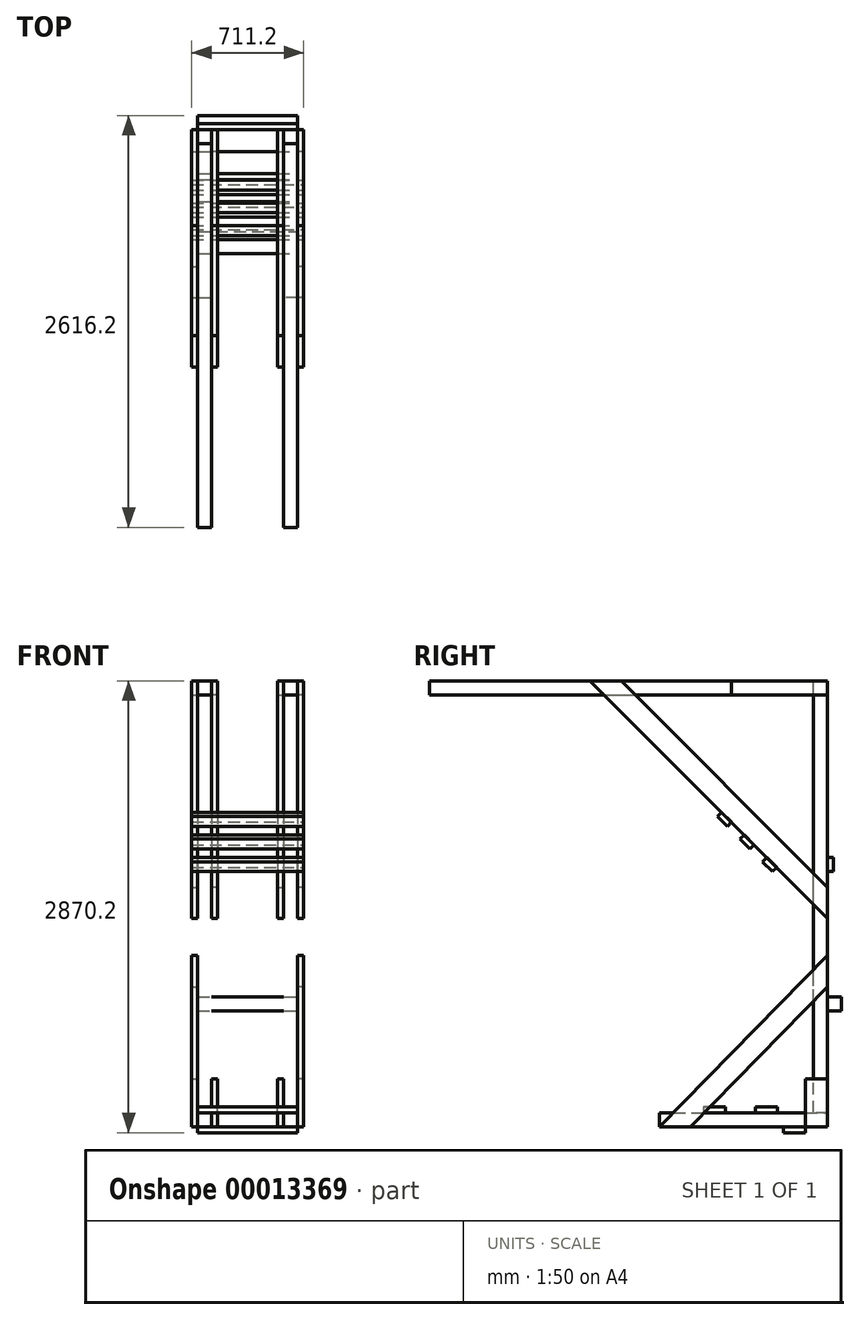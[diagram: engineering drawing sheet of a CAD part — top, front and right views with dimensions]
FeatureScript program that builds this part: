
annotation { "Feature Type Name" : "Feature", "Feature Type Description" : "" }
export const myFeature = defineFeature(function(context is Context, id is Id, definition is map)
    precondition{}
    {
        {
            var Q0;
            Q0=qCreatedBy(makeId("Top.planeOp"),FACE);
            var sketch = newSketch(context, id + "F0", { "sketchPlane" : qUnion([Q0])});
            skLineSegment(sketch, "E0.bottom", {"start": v(-317.5, 0) * mm, "end": v(-228.6, 0) * mm});
            skLineSegment(sketch, "E0.top", {"start": v(-317.5, -88.9) * mm, "end": v(-228.6, -88.9) * mm});
            skLineSegment(sketch, "E0.left", {"start": v(-317.5, 0) * mm, "end": v(-317.5, -88.9) * mm});
            skLineSegment(sketch, "E0.right", {"start": v(-228.6, 0) * mm, "end": v(-228.6, -88.9) * mm});
            skSolve(sketch);
        }
        {
            var Q0;
            Q0=qSketchRegion(id+"F0",true);
            extrude(context, id + "F1", {"entities" : qUnion([Q0]), "oppositeDirection" : true, "depth" : 2743.2 * mm});
        }
        {
            var Q0;
            Q0=makeQuery(id+"F1.opExtrude","SWEPT_FACE",FACE,{"disambiguationData":[OSD([sQuery(id+"F0.wireOp",EDGE,"E0.bottom")])]});
            var sketch = newSketch(context, id + "F2", { "sketchPlane" : qUnion([Q0])});
            skLineSegment(sketch, "E1.bottom", {"start": v(317.5, -2832.1) * mm, "end": v(228.6, -2832.1) * mm});
            skLineSegment(sketch, "E1.top", {"start": v(317.5, -2743.2) * mm, "end": v(228.6, -2743.2) * mm});
            skLineSegment(sketch, "E1.left", {"start": v(228.6, -2832.1) * mm, "end": v(228.6, -2743.2) * mm});
            skLineSegment(sketch, "E1.right", {"start": v(317.5, -2832.1) * mm, "end": v(317.5, -2743.2) * mm});
            skSolve(sketch);
        }
        {
            var Q0;
            Q0=makeQuery(id+"F2.imprint","IMPRINT",FACE,{"disambiguationData":[TD([[makeQuery(id+"F2.imprint","IMPRINT",EDGE,{"derivedFrom":sQuery(id+"F2.wireOp",EDGE,"E1.bottom")}),-1.0]])]});
            extrude(context, id + "F3", {"entities" : qUnion([Q0]), "oppositeDirection" : true, "depth" : 1066.8 * mm});
        }
        {
            var Q0;
            Q0=makeQuery(id+"F1.opExtrude","SWEPT_FACE",FACE,{"disambiguationData":[OSD([sQuery(id+"F0.wireOp",EDGE,"E0.right")])]});
            var sketch = newSketch(context, id + "F4", { "sketchPlane" : qUnion([Q0])});
            skLineSegment(sketch, "E2.bottom", {"start": v(0, -2832.1) * mm, "end": v(-139.7, -2832.1) * mm});
            skLineSegment(sketch, "E2.top", {"start": v(0, -2527.3) * mm, "end": v(-139.7, -2527.3) * mm});
            skLineSegment(sketch, "E2.left", {"start": v(0, -2832.1) * mm, "end": v(0, -2527.3) * mm});
            skLineSegment(sketch, "E2.right", {"start": v(-139.7, -2832.1) * mm, "end": v(-139.7, -2527.3) * mm});
            skSolve(sketch);
        }
        {
            var Q0;
            {var subQ5=sQuery(id+"F4.wireOp",EDGE,"E2.right");Q0=makeQuery(id+"F4.imprint","IMPRINT",FACE,{"disambiguationData":[TD([[makeQuery(id+"F4.imprint","IMPRINT",EDGE,{"derivedFrom":subQ5}),-1.0]])]});}
            var Q1;
            {var subQ6=sQuery(id+"F4.wireOp",EDGE,"E2.left");Q1=makeQuery(id+"F4.imprint","IMPRINT",FACE,{"disambiguationData":[TD([[makeQuery(id+"F4.imprint","IMPRINT",EDGE,{"derivedFrom":subQ6}),1.0]])]});}
            extrude(context, id + "F5", {"entities" : qUnion([Q0, Q1]), "depth" : 38.1 * mm});
        }
        {
            var Q0;
            Q0=makeQuery(id+"F1.opExtrude","SWEPT_FACE",FACE,{"disambiguationData":[OSD([sQuery(id+"F0.wireOp",EDGE,"E0.top")])]});
            var sketch = newSketch(context, id + "F6", { "sketchPlane" : qUnion([Q0])});
            skLineSegment(sketch, "E3.bottom", {"start": v(-317.5, 0) * mm, "end": v(-228.6, 0) * mm});
            skLineSegment(sketch, "E3.top", {"start": v(-317.5, -88.9) * mm, "end": v(-228.6, -88.9) * mm});
            skLineSegment(sketch, "E3.left", {"start": v(-317.5, 0) * mm, "end": v(-317.5, -88.9) * mm});
            skLineSegment(sketch, "E3.right", {"start": v(-228.6, 0) * mm, "end": v(-228.6, -88.9) * mm});
            skSolve(sketch);
        }
        {
            var Q0;
            Q0=makeQuery(id+"F6.imprint","IMPRINT",FACE,{"disambiguationData":[TD([[makeQuery(id+"F6.imprint","IMPRINT",EDGE,{"derivedFrom":sQuery(id+"F6.wireOp",EDGE,"E3.bottom")}),-1.0]])]});
            extrude(context, id + "F7", {"entities" : qUnion([Q0]), "depth" : 2438.4 * mm});
        }
        {
            var Q0;
            Q0=makeQuery(id+"F1.opExtrude","SWEPT_FACE",FACE,{"disambiguationData":[OSD([sQuery(id+"F0.wireOp",EDGE,"E0.right")])]});
            var sketch = newSketch(context, id + "F8", { "sketchPlane" : qUnion([Q0])});
            skLineSegment(sketch, "E4.bottom", {"start": v(0, 0) * mm, "end": v(-609.6, 0) * mm});
            skLineSegment(sketch, "E4.top", {"start": v(0, -88.9) * mm, "end": v(-609.6, -88.9) * mm});
            skLineSegment(sketch, "E4.left", {"start": v(0, 0) * mm, "end": v(0, -88.9) * mm});
            skLineSegment(sketch, "E4.right", {"start": v(-609.6, 0) * mm, "end": v(-609.6, -88.9) * mm});
            skLineSegment(sketch, "E5.0", {"start": v(-2527.3, -88.9) * mm, "end": v(-88.9, -88.9) * mm, "construction": true});
            skSolve(sketch);
        }
        {
            var Q0;
            {var subQ5=sQuery(id+"F8.wireOp",EDGE,"E4.right");Q0=makeQuery(id+"F8.imprint","IMPRINT",FACE,{"disambiguationData":[TD([[makeQuery(id+"F8.imprint","IMPRINT",EDGE,{"derivedFrom":subQ5}),1.0]])]});}
            var Q1;
            {var subQ6=sQuery(id+"F8.wireOp",EDGE,"E4.left");Q1=makeQuery(id+"F8.imprint","IMPRINT",FACE,{"disambiguationData":[TD([[makeQuery(id+"F8.imprint","IMPRINT",EDGE,{"derivedFrom":subQ6}),1.0]])]});}
            extrude(context, id + "F9", {"entities" : qUnion([Q0, Q1]), "depth" : 38.1 * mm});
        }
        {
            var Q0;
            Q0=makeQuery(id+"F7.opExtrude","SWEPT_FACE",FACE,{"disambiguationData":[OSD([sQuery(id+"F6.wireOp",EDGE,"E3.right")])]});
            var sketch = newSketch(context, id + "F10", { "sketchPlane" : qUnion([Q0])});
            skLineSegment(sketch, "E6.0", {"start": v(0, -2743.2) * mm, "end": v(0, 0) * mm, "construction": true});
            skLineSegment(sketch, "E7", {"start": v(-1508.68, 0) * mm, "end": v(0, -1508.68) * mm});
            skLineSegment(sketch, "E8", {"start": v(0, -1508.68) * mm, "end": v(0, -1311.12) * mm});
            skLineSegment(sketch, "E9", {"start": v(0, -1311.12) * mm, "end": v(-1311.12, 0) * mm});
            skLineSegment(sketch, "E10", {"start": v(-1311.12, 0) * mm, "end": v(-1508.68, 0) * mm});
            skLineSegment(sketch, "E11", {"start": v(-1311.12, 0) * mm, "end": v(0, 0) * mm, "construction": true});
            skLineSegment(sketch, "E12", {"start": v(0, -1311.12) * mm, "end": v(0, 0) * mm, "construction": true});
            skSolve(sketch);
        }
        {
            var Q0;
            Q0=makeQuery(id+"F7.opExtrude","SWEPT_FACE",FACE,{"disambiguationData":[OSD([sQuery(id+"F6.wireOp",EDGE,"E3.right")])]});
            var Q1;
            Q1=makeQuery(id+"F7.opExtrude","SWEPT_FACE",FACE,{"disambiguationData":[OSD([sQuery(id+"F6.wireOp",EDGE,"E3.left")])]});
            cPlane(context, id + "F11", {"entities" : qUnion([Q0, Q1]), "cplaneType" : CPlaneType.MID_PLANE, "offset" : 152.4 * mm, "width" : 152.4 * mm, "height" : 152.4 * mm});
        }
        {
            var Q0;
            {var subQ5=sQuery(id+"F10.wireOp",EDGE,"E8");Q0=makeQuery(id+"F10.imprint","IMPRINT",FACE,{"disambiguationData":[TD([[makeQuery(id+"F10.imprint","IMPRINT",EDGE,{"derivedFrom":subQ5}),1.0]])]});}
            var Q1;
            {var subQ6=sQuery(id+"F10.wireOp",EDGE,"E10");Q1=makeQuery(id+"F10.imprint","IMPRINT",FACE,{"disambiguationData":[TD([[makeQuery(id+"F10.imprint","IMPRINT",EDGE,{"derivedFrom":subQ6}),-1.0]])]});}
            extrude(context, id + "F12", {"entities" : qUnion([Q0, Q1]), "depth" : 38.1 * mm});
        }
        {
            var Q0;
            Q0=makeQuery(id+"F9.opExtrude","SWEPT_BODY",BODY,{"disambiguationData":[OSD([sQuery(id+"F8.wireOp",EDGE,"E4.bottom"),sQuery(id+"F8.wireOp",EDGE,"E4.top"),sQuery(id+"F8.wireOp",EDGE,"E4.left"),sQuery(id+"F8.wireOp",EDGE,"E4.right")])]});
            var Q1;
            Q1=makeQuery(id+"F5.opExtrude","SWEPT_BODY",BODY,{"disambiguationData":[OSD([sQuery(id+"F4.wireOp",EDGE,"E2.bottom"),sQuery(id+"F4.wireOp",EDGE,"E2.top"),sQuery(id+"F4.wireOp",EDGE,"E2.left"),sQuery(id+"F4.wireOp",EDGE,"E2.right")])]});
            var Q2;
            Q2=makeQuery(id+"F12.opExtrude","SWEPT_BODY",BODY,{"disambiguationData":[OSD([sQuery(id+"F10.wireOp",EDGE,"E7"),sQuery(id+"F10.wireOp",EDGE,"E8"),sQuery(id+"F10.wireOp",EDGE,"E9"),sQuery(id+"F10.wireOp",EDGE,"E10")])]});
            var Q3;
            Q3=qCreatedBy(id+"F11.planeOp",FACE);
            mirror(context, id + "F13", {"entities" : qUnion([Q0, Q1, Q2]), "mirrorPlane" : qUnion([Q3])});
        }
        {
            var Q0;
            Q0=makeQuery(id+"F1.opExtrude","SWEPT_FACE",FACE,{"disambiguationData":[OSD([sQuery(id+"F0.wireOp",EDGE,"E0.left")])]});
            var sketch = newSketch(context, id + "F14", { "sketchPlane" : qUnion([Q0])});
            skLineSegment(sketch, "E13.0", {"start": v(1066.8, -2832.1) * mm, "end": v(0, -2832.1) * mm, "construction": true});
            skLineSegment(sketch, "E14", {"start": v(0, -1943.32) * mm, "end": v(871.18, -2832.1) * mm});
            skLineSegment(sketch, "E15", {"start": v(871.18, -2832.1) * mm, "end": v(1066.8, -2832.1) * mm});
            skLineSegment(sketch, "E16", {"start": v(1066.8, -2832.1) * mm, "end": v(0, -1743.75) * mm});
            skLineSegment(sketch, "E17", {"start": v(0, -1743.75) * mm, "end": v(0, -1943.32) * mm});
            skSolve(sketch);
        }
        {
            var Q0;
            {var subQ5=sQuery(id+"F14.wireOp",EDGE,"E15");Q0=makeQuery(id+"F14.imprint","IMPRINT",FACE,{"disambiguationData":[TD([[makeQuery(id+"F14.imprint","IMPRINT",EDGE,{"derivedFrom":subQ5}),1.0]])]});}
            var Q1;
            {var subQ6=sQuery(id+"F14.wireOp",EDGE,"E17");Q1=makeQuery(id+"F14.imprint","IMPRINT",FACE,{"disambiguationData":[TD([[makeQuery(id+"F14.imprint","IMPRINT",EDGE,{"derivedFrom":subQ6}),-1.0]])]});}
            extrude(context, id + "F15", {"entities" : qUnion([Q0, Q1]), "depth" : 38.1 * mm});
        }
        {
            var Q0;
            Q0=makeQuery(id+"F1.opExtrude","SWEPT_BODY",BODY,{"disambiguationData":[OSD([sQuery(id+"F0.wireOp",EDGE,"E0.bottom"),sQuery(id+"F0.wireOp",EDGE,"E0.top"),sQuery(id+"F0.wireOp",EDGE,"E0.left"),sQuery(id+"F0.wireOp",EDGE,"E0.right")])]});
            var Q1;
            Q1=makeQuery(id+"F3.opExtrude","SWEPT_BODY",BODY,{"disambiguationData":[OSD([sQuery(id+"F2.wireOp",EDGE,"E1.bottom"),sQuery(id+"F2.wireOp",EDGE,"E1.top"),sQuery(id+"F2.wireOp",EDGE,"E1.left"),sQuery(id+"F2.wireOp",EDGE,"E1.right")])]});
            var Q2;
            Q2=makeQuery(id+"F5.opExtrude","SWEPT_BODY",BODY,{"disambiguationData":[OSD([sQuery(id+"F4.wireOp",EDGE,"E2.bottom"),sQuery(id+"F4.wireOp",EDGE,"E2.top"),sQuery(id+"F4.wireOp",EDGE,"E2.left"),sQuery(id+"F4.wireOp",EDGE,"E2.right")])]});
            var Q3;
            Q3=makeQuery(id+"F7.opExtrude","SWEPT_BODY",BODY,{"disambiguationData":[OSD([sQuery(id+"F6.wireOp",EDGE,"E3.bottom"),sQuery(id+"F6.wireOp",EDGE,"E3.top"),sQuery(id+"F6.wireOp",EDGE,"E3.left"),sQuery(id+"F6.wireOp",EDGE,"E3.right")])]});
            var Q4;
            Q4=makeQuery(id+"F9.opExtrude","SWEPT_BODY",BODY,{"disambiguationData":[OSD([sQuery(id+"F8.wireOp",EDGE,"E4.bottom"),sQuery(id+"F8.wireOp",EDGE,"E4.top"),sQuery(id+"F8.wireOp",EDGE,"E4.left"),sQuery(id+"F8.wireOp",EDGE,"E4.right")])]});
            var Q5;
            Q5=makeQuery(id+"F13.opPattern","COPY",BODY,{"derivedFrom":makeQuery(id+"F9.opExtrude","SWEPT_BODY",BODY,{"disambiguationData":[OSD([sQuery(id+"F8.wireOp",EDGE,"E4.bottom"),sQuery(id+"F8.wireOp",EDGE,"E4.top"),sQuery(id+"F8.wireOp",EDGE,"E4.left"),sQuery(id+"F8.wireOp",EDGE,"E4.right")])]}),"instanceName":"1"});
            var Q6;
            Q6=makeQuery(id+"F13.opPattern","COPY",BODY,{"derivedFrom":makeQuery(id+"F5.opExtrude","SWEPT_BODY",BODY,{"disambiguationData":[OSD([sQuery(id+"F4.wireOp",EDGE,"E2.bottom"),sQuery(id+"F4.wireOp",EDGE,"E2.top"),sQuery(id+"F4.wireOp",EDGE,"E2.left"),sQuery(id+"F4.wireOp",EDGE,"E2.right")])]}),"instanceName":"1"});
            var Q7;
            Q7=makeQuery(id+"F15.opExtrude","SWEPT_BODY",BODY,{"disambiguationData":[OSD([sQuery(id+"F14.wireOp",EDGE,"E14"),sQuery(id+"F14.wireOp",EDGE,"E15"),sQuery(id+"F14.wireOp",EDGE,"E16"),sQuery(id+"F14.wireOp",EDGE,"E17")])]});
            var Q8;
            Q8=makeQuery(id+"F13.opPattern","COPY",BODY,{"derivedFrom":makeQuery(id+"F12.opExtrude","SWEPT_BODY",BODY,{"disambiguationData":[OSD([sQuery(id+"F10.wireOp",EDGE,"E7"),sQuery(id+"F10.wireOp",EDGE,"E8"),sQuery(id+"F10.wireOp",EDGE,"E9"),sQuery(id+"F10.wireOp",EDGE,"E10")])]}),"instanceName":"1"});
            var Q9;
            Q9=makeQuery(id+"F12.opExtrude","SWEPT_BODY",BODY,{"disambiguationData":[OSD([sQuery(id+"F10.wireOp",EDGE,"E7"),sQuery(id+"F10.wireOp",EDGE,"E8"),sQuery(id+"F10.wireOp",EDGE,"E9"),sQuery(id+"F10.wireOp",EDGE,"E10")])]});
            var Q10;
            Q10=qCreatedBy(makeId("Right.planeOp"),FACE);
            mirror(context, id + "F16", {"entities" : qUnion([Q0, Q1, Q2, Q3, Q4, Q5, Q6, Q7, Q8, Q9]), "mirrorPlane" : qUnion([Q10])});
        }
        {
            var Q0;
            Q0=makeQuery(id+"F3.opExtrude","SWEPT_FACE",FACE,{"disambiguationData":[OSD([sQuery(id+"F2.wireOp",EDGE,"E1.top")])]});
            var sketch = newSketch(context, id + "F17", { "sketchPlane" : qUnion([Q0])});
            skLineSegment(sketch, "E18.bottom", {"start": v(-317.5, -317.5) * mm, "end": v(317.5, -317.5) * mm});
            skLineSegment(sketch, "E18.top", {"start": v(-317.5, -457.2) * mm, "end": v(317.5, -457.2) * mm});
            skLineSegment(sketch, "E18.left", {"start": v(-317.5, -317.5) * mm, "end": v(-317.5, -457.2) * mm});
            skLineSegment(sketch, "E18.right", {"start": v(317.5, -317.5) * mm, "end": v(317.5, -457.2) * mm});
            skLineSegment(sketch, "E19.bottom", {"start": v(-317.5, -647.7) * mm, "end": v(317.5, -647.7) * mm});
            skLineSegment(sketch, "E19.top", {"start": v(-317.5, -787.4) * mm, "end": v(317.5, -787.4) * mm});
            skLineSegment(sketch, "E19.left", {"start": v(-317.5, -647.7) * mm, "end": v(-317.5, -787.4) * mm});
            skLineSegment(sketch, "E19.right", {"start": v(317.5, -647.7) * mm, "end": v(317.5, -787.4) * mm});
            skSolve(sketch);
        }
        {
            var Q0;
            Q0=qSketchRegion(id+"F17",true);
            extrude(context, id + "F18", {"entities" : qUnion([Q0]), "depth" : 38.1 * mm});
        }
        {
            var Q0;
            Q0=makeQuery(id+"F3.opExtrude","SWEPT_FACE",FACE,{"disambiguationData":[OSD([sQuery(id+"F2.wireOp",EDGE,"E1.bottom")])]});
            var sketch = newSketch(context, id + "F19", { "sketchPlane" : qUnion([Q0])});
            skLineSegment(sketch, "E20.bottom", {"start": v(-317.5, 139.7) * mm, "end": v(317.5, 139.7) * mm});
            skLineSegment(sketch, "E20.top", {"start": v(-317.5, 279.4) * mm, "end": v(317.5, 279.4) * mm});
            skLineSegment(sketch, "E20.left", {"start": v(-317.5, 139.7) * mm, "end": v(-317.5, 279.4) * mm});
            skLineSegment(sketch, "E20.right", {"start": v(317.5, 139.7) * mm, "end": v(317.5, 279.4) * mm});
            skSolve(sketch);
        }
        {
            var Q0;
            Q0=qSketchRegion(id+"F19",true);
            extrude(context, id + "F20", {"entities" : qUnion([Q0]), "depth" : 38.1 * mm});
        }
        {
            var Q0;
            Q0=makeQuery(id+"F1.opExtrude","SWEPT_FACE",FACE,{"disambiguationData":[OSD([sQuery(id+"F0.wireOp",EDGE,"E0.bottom")])]});
            var sketch = newSketch(context, id + "F21", { "sketchPlane" : qUnion([Q0])});
            skLineSegment(sketch, "E21.bottom", {"start": v(317.5, -2006.6) * mm, "end": v(-317.5, -2006.6) * mm});
            skLineSegment(sketch, "E21.top", {"start": v(317.5, -2095.5) * mm, "end": v(-317.5, -2095.5) * mm});
            skLineSegment(sketch, "E21.left", {"start": v(317.5, -2006.6) * mm, "end": v(317.5, -2095.5) * mm});
            skLineSegment(sketch, "E21.right", {"start": v(-317.5, -2006.6) * mm, "end": v(-317.5, -2095.5) * mm});
            skSolve(sketch);
        }
        {
            var Q0;
            Q0=qSketchRegion(id+"F21",true);
            extrude(context, id + "F22", {"entities" : qUnion([Q0]), "depth" : 88.9 * mm});
        }
        {
            var Q0;
            Q0=makeQuery(id+"F13.opPattern","COPY",FACE,{"derivedFrom":makeQuery(id+"F12.opExtrude","SWEPT_FACE",FACE,{"disambiguationData":[OSD([sQuery(id+"F10.wireOp",EDGE,"E7")])]}),"instanceName":"1"});
            var sketch = newSketch(context, id + "F23", { "sketchPlane" : qUnion([Q0])});
            skLineSegment(sketch, "E22.bottom", {"start": v(-355.6, -609.6) * mm, "end": v(355.6, -609.6) * mm});
            skLineSegment(sketch, "E22.top", {"start": v(-355.6, -520.7) * mm, "end": v(355.6, -520.7) * mm});
            skLineSegment(sketch, "E22.left", {"start": v(-355.6, -609.6) * mm, "end": v(-355.6, -520.7) * mm});
            skLineSegment(sketch, "E22.right", {"start": v(355.6, -609.6) * mm, "end": v(355.6, -520.7) * mm});
            skLineSegment(sketch, "E23.0.1.0", {"start": v(-355.6, -406.4) * mm, "end": v(355.6, -406.4) * mm});
            skLineSegment(sketch, "E23.0.1.1", {"start": v(-355.6, -317.5) * mm, "end": v(355.6, -317.5) * mm});
            skLineSegment(sketch, "E23.0.1.2", {"start": v(355.6, -406.4) * mm, "end": v(355.6, -317.5) * mm});
            skLineSegment(sketch, "E23.0.1.3", {"start": v(-355.6, -406.4) * mm, "end": v(-355.6, -317.5) * mm});
            skLineSegment(sketch, "E23.0.2.0", {"start": v(-355.6, -203.2) * mm, "end": v(355.6, -203.2) * mm});
            skLineSegment(sketch, "E23.0.2.1", {"start": v(-355.6, -114.3) * mm, "end": v(355.6, -114.3) * mm});
            skLineSegment(sketch, "E23.0.2.2", {"start": v(355.6, -203.2) * mm, "end": v(355.6, -114.3) * mm});
            skLineSegment(sketch, "E23.0.2.3", {"start": v(-355.6, -203.2) * mm, "end": v(-355.6, -114.3) * mm});
            skLineSegment(sketch, "E23.direction1", {"start": v(-355.6, -609.6) * mm, "end": v(-330.2, -609.6) * mm, "construction": true});
            skLineSegment(sketch, "E23.direction2", {"start": v(-355.6, -609.6) * mm, "end": v(-355.6, -406.4) * mm, "construction": true});
            skSolve(sketch);
        }
        {
            var Q0;
            Q0=qSketchRegion(id+"F23",true);
            extrude(context, id + "F24", {"entities" : qUnion([Q0]), "depth" : 38.1 * mm});
        }
        {
            var Q0;
            Q0=makeQuery(id+"F1.opExtrude","SWEPT_FACE",FACE,{"disambiguationData":[OSD([sQuery(id+"F0.wireOp",EDGE,"E0.bottom")])]});
            var sketch = newSketch(context, id + "F25", { "sketchPlane" : qUnion([Q0])});
            skLineSegment(sketch, "E24.bottom", {"start": v(317.5, -1212.33) * mm, "end": v(-317.5, -1212.33) * mm});
            skLineSegment(sketch, "E24.top", {"start": v(317.5, -1123.43) * mm, "end": v(-317.5, -1123.43) * mm});
            skLineSegment(sketch, "E24.left", {"start": v(317.5, -1212.33) * mm, "end": v(317.5, -1123.43) * mm});
            skLineSegment(sketch, "E24.right", {"start": v(-317.5, -1212.33) * mm, "end": v(-317.5, -1123.43) * mm});
            skSolve(sketch);
        }
        {
            var Q0;
            Q0=qSketchRegion(id+"F25",true);
            extrude(context, id + "F26", {"entities" : qUnion([Q0]), "depth" : 38.1 * mm});
        }
    });
